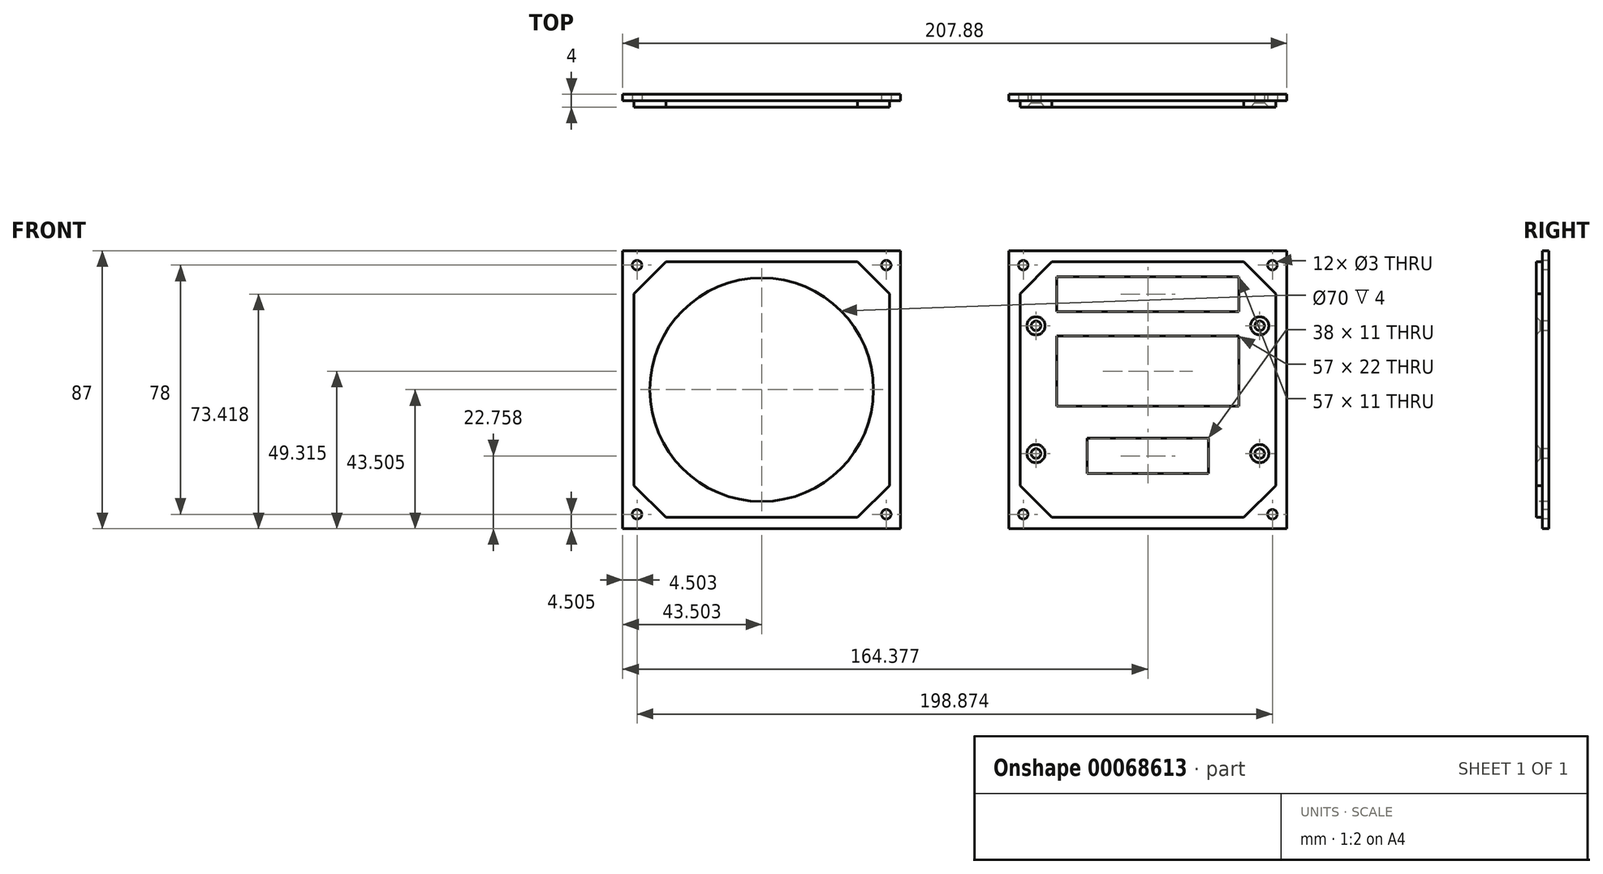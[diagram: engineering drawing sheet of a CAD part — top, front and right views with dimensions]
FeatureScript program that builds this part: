
annotation { "Feature Type Name" : "Feature", "Feature Type Description" : "" }
export const myFeature = defineFeature(function(context is Context, id is Id, definition is map)
    precondition{}
    {
        {
            var Q0;
            Q0=qCreatedBy(makeId("Front.planeOp"),FACE);
            cPlane(context, id + "F0", {"entities" : qUnion([Q0]), "cplaneType" : CPlaneType.OFFSET, "offset" : 5 * mm, "width" : 150 * mm, "height" : 150 * mm});
        }
        {
            var Q0;
            Q0=qCreatedBy(id+"F0.planeOp",FACE);
            var sketch = newSketch(context, id + "F1", { "sketchPlane" : qUnion([Q0])});
            skLineSegment(sketch, "E0.0", {"start": v(-50.26, 263.3) * mm, "end": v(-50.26, 233.3) * mm});
            skLineSegment(sketch, "E0.1", {"start": v(-50.26, 203.3) * mm, "end": v(-60.26, 193.3) * mm});
            skLineSegment(sketch, "E0.2", {"start": v(-60.26, 193.3) * mm, "end": v(-90.26, 193.3) * mm});
            skLineSegment(sketch, "E0.3", {"start": v(-120.26, 193.3) * mm, "end": v(-130.26, 203.3) * mm});
            skLineSegment(sketch, "E0.4", {"start": v(-130.26, 203.3) * mm, "end": v(-130.26, 233.3) * mm});
            skLineSegment(sketch, "E0.5", {"start": v(-130.26, 263.3) * mm, "end": v(-120.26, 273.3) * mm});
            skLineSegment(sketch, "E0.6", {"start": v(-120.26, 273.3) * mm, "end": v(-90.26, 273.3) * mm});
            skLineSegment(sketch, "E0.7", {"start": v(-60.26, 273.3) * mm, "end": v(-50.26, 263.3) * mm});
            skPoint(sketch, "E1", {"position": v(-90.26, 233.3) * mm});
            skLineSegment(sketch, "E2", {"start": v(-90.26, 273.3) * mm, "end": v(-60.26, 273.3) * mm});
            skLineSegment(sketch, "E3", {"start": v(-130.26, 233.3) * mm, "end": v(-130.26, 263.3) * mm});
            skLineSegment(sketch, "E4", {"start": v(-50.26, 233.3) * mm, "end": v(-50.26, 203.3) * mm});
            skLineSegment(sketch, "E5", {"start": v(-90.26, 193.3) * mm, "end": v(-120.26, 193.3) * mm});
            skSolve(sketch);
        }
        {
            var Q0;
            Q0=qSketchRegion(id+"F1",true);
            extrude(context, id + "F2", {"entities" : qUnion([Q0]), "depth" : 2 * mm});
        }
        {
            var Q0;
            Q0=makeQuery(id+"F2.opExtrude","CAP_FACE",FACE,{"disambiguationData":[OSD([sQuery(id+"F1.wireOp",EDGE,"E0.0"),sQuery(id+"F1.wireOp",EDGE,"E0.1"),sQuery(id+"F1.wireOp",EDGE,"E0.2"),sQuery(id+"F1.wireOp",EDGE,"E0.3"),sQuery(id+"F1.wireOp",EDGE,"E0.4"),sQuery(id+"F1.wireOp",EDGE,"E0.5"),sQuery(id+"F1.wireOp",EDGE,"E0.6"),sQuery(id+"F1.wireOp",EDGE,"E0.7"),sQuery(id+"F1.wireOp",EDGE,"E2"),sQuery(id+"F1.wireOp",EDGE,"E3"),sQuery(id+"F1.wireOp",EDGE,"E4"),sQuery(id+"F1.wireOp",EDGE,"E5")])],"isStart":true});
            var sketch = newSketch(context, id + "F3", { "sketchPlane" : qUnion([Q0])});
            skLineSegment(sketch, "E6.bottom", {"start": v(133.76, 276.8) * mm, "end": v(46.76, 276.8) * mm});
            skLineSegment(sketch, "E6.top", {"start": v(133.76, 189.8) * mm, "end": v(46.76, 189.8) * mm});
            skLineSegment(sketch, "E6.left", {"start": v(133.76, 276.8) * mm, "end": v(133.76, 189.8) * mm});
            skLineSegment(sketch, "E6.right", {"start": v(46.76, 276.8) * mm, "end": v(46.76, 189.8) * mm});
            skSolve(sketch);
        }
        {
            var Q0;
            Q0=qSketchRegion(id+"F3",true);
            extrude(context, id + "F4", {"entities" : qUnion([Q0]), "operationType" : NewBodyOperationType.ADD, "depth" : 2 * mm});
        }
        {
            var Q0;
            Q0=makeQuery(id+"F2.opExtrude","CAP_FACE",FACE,{"disambiguationData":[OSD([sQuery(id+"F1.wireOp",EDGE,"E0.0"),sQuery(id+"F1.wireOp",EDGE,"E0.1"),sQuery(id+"F1.wireOp",EDGE,"E0.2"),sQuery(id+"F1.wireOp",EDGE,"E0.3"),sQuery(id+"F1.wireOp",EDGE,"E0.4"),sQuery(id+"F1.wireOp",EDGE,"E0.5"),sQuery(id+"F1.wireOp",EDGE,"E0.6"),sQuery(id+"F1.wireOp",EDGE,"E0.7"),sQuery(id+"F1.wireOp",EDGE,"E2"),sQuery(id+"F1.wireOp",EDGE,"E3"),sQuery(id+"F1.wireOp",EDGE,"E4"),sQuery(id+"F1.wireOp",EDGE,"E5")])],"isStart":false});
            var sketch = newSketch(context, id + "F5", { "sketchPlane" : qUnion([Q0])});
            skCircle(sketch, "E7", {"center": v(-90.26, 233.3) * mm, "radius": 35 * mm});
            skCircle(sketch, "E8", {"center": v(-129.26, 272.3) * mm, "radius": 1.5 * mm});
            skCircle(sketch, "E9", {"center": v(-51.26, 272.3) * mm, "radius": 1.5 * mm});
            skCircle(sketch, "E10", {"center": v(-129.26, 194.3) * mm, "radius": 1.5 * mm});
            skCircle(sketch, "E11", {"center": v(-51.26, 194.3) * mm, "radius": 1.5 * mm});
            skSolve(sketch);
        }
        {
            var Q0;
            Q0=sQuery(id+"F5.wireOp",VERTEX,"E8.center");
            var Q1;
            Q1=sQuery(id+"F5.wireOp",VERTEX,"E9.center");
            var Q2;
            Q2=sQuery(id+"F5.wireOp",VERTEX,"E11.center");
            var Q3;
            Q3=sQuery(id+"F5.wireOp",VERTEX,"E10.center");
            var Q4;
            Q4=makeQuery(id+"F2.opExtrude","SWEPT_BODY",BODY,{"disambiguationData":[OSD([sQuery(id+"F1.wireOp",EDGE,"E0.0"),sQuery(id+"F1.wireOp",EDGE,"E0.1"),sQuery(id+"F1.wireOp",EDGE,"E0.2"),sQuery(id+"F1.wireOp",EDGE,"E0.3"),sQuery(id+"F1.wireOp",EDGE,"E0.4"),sQuery(id+"F1.wireOp",EDGE,"E0.5"),sQuery(id+"F1.wireOp",EDGE,"E0.6"),sQuery(id+"F1.wireOp",EDGE,"E0.7"),sQuery(id+"F1.wireOp",EDGE,"E2"),sQuery(id+"F1.wireOp",EDGE,"E3"),sQuery(id+"F1.wireOp",EDGE,"E4"),sQuery(id+"F1.wireOp",EDGE,"E5")])]});
            hole(context, id + "F6", {"style" : HoleStyle.SIMPLE, "endStyle" : HoleEndStyle.THROUGH, "holeDiameter" : 3 * mm, "locations" : qUnion([Q0, Q1, Q2, Q3]), "scope" : qUnion([Q4]), "isTappedThrough" : true});
        }
        {
            var Q0;
            Q0=sQuery(id+"F5.wireOp",VERTEX,"E7.center");
            var Q1;
            Q1=makeQuery(id+"F2.opExtrude","SWEPT_BODY",BODY,{"disambiguationData":[OSD([sQuery(id+"F1.wireOp",EDGE,"E0.0"),sQuery(id+"F1.wireOp",EDGE,"E0.1"),sQuery(id+"F1.wireOp",EDGE,"E0.2"),sQuery(id+"F1.wireOp",EDGE,"E0.3"),sQuery(id+"F1.wireOp",EDGE,"E0.4"),sQuery(id+"F1.wireOp",EDGE,"E0.5"),sQuery(id+"F1.wireOp",EDGE,"E0.6"),sQuery(id+"F1.wireOp",EDGE,"E0.7"),sQuery(id+"F1.wireOp",EDGE,"E2"),sQuery(id+"F1.wireOp",EDGE,"E3"),sQuery(id+"F1.wireOp",EDGE,"E4"),sQuery(id+"F1.wireOp",EDGE,"E5")])]});
            hole(context, id + "F7", {"style" : HoleStyle.SIMPLE, "endStyle" : HoleEndStyle.THROUGH, "holeDiameter" : 70 * mm, "locations" : qUnion([Q0]), "scope" : qUnion([Q1]), "isTappedThrough" : true});
        }
        {
            var Q0;
            Q0=qCreatedBy(id+"F0.planeOp",FACE);
            var sketch = newSketch(context, id + "F8", { "sketchPlane" : qUnion([Q0])});
            skLineSegment(sketch, "E12.0", {"start": v(70.62, 263.3) * mm, "end": v(70.62, 233.3) * mm});
            skLineSegment(sketch, "E12.1", {"start": v(70.62, 203.3) * mm, "end": v(60.62, 193.3) * mm});
            skLineSegment(sketch, "E12.2", {"start": v(60.62, 193.3) * mm, "end": v(30.62, 193.3) * mm});
            skLineSegment(sketch, "E12.3", {"start": v(0.62, 193.3) * mm, "end": v(-9.38, 203.3) * mm});
            skLineSegment(sketch, "E12.4", {"start": v(-9.38, 203.3) * mm, "end": v(-9.38, 233.3) * mm});
            skLineSegment(sketch, "E12.5", {"start": v(-9.38, 263.3) * mm, "end": v(0.62, 273.3) * mm});
            skLineSegment(sketch, "E12.6", {"start": v(0.62, 273.3) * mm, "end": v(30.62, 273.3) * mm});
            skLineSegment(sketch, "E12.7", {"start": v(60.62, 273.3) * mm, "end": v(70.62, 263.3) * mm});
            skPoint(sketch, "E13", {"position": v(30.62, 233.3) * mm});
            skLineSegment(sketch, "E14", {"start": v(30.62, 273.3) * mm, "end": v(60.62, 273.3) * mm});
            skLineSegment(sketch, "E15", {"start": v(-9.38, 233.3) * mm, "end": v(-9.38, 263.3) * mm});
            skLineSegment(sketch, "E16", {"start": v(70.62, 233.3) * mm, "end": v(70.62, 203.3) * mm});
            skLineSegment(sketch, "E17", {"start": v(30.62, 193.3) * mm, "end": v(0.62, 193.3) * mm});
            skSolve(sketch);
        }
        {
            var Q0;
            Q0 = qSketchRegion(id + "F8", true);
            extrude(context, id + "F9", {"entities" : qUnion([Q0]), "depth" : 2 * mm});
        }
        {
            var Q0;
            Q0=makeQuery(id+"F9.opExtrude","CAP_FACE",FACE,{"disambiguationData":[OSD([sQuery(id+"F8.wireOp",EDGE,"E12.0"),sQuery(id+"F8.wireOp",EDGE,"E12.1"),sQuery(id+"F8.wireOp",EDGE,"E12.2"),sQuery(id+"F8.wireOp",EDGE,"E12.3"),sQuery(id+"F8.wireOp",EDGE,"E12.4"),sQuery(id+"F8.wireOp",EDGE,"E12.5"),sQuery(id+"F8.wireOp",EDGE,"E12.6"),sQuery(id+"F8.wireOp",EDGE,"E12.7"),sQuery(id+"F8.wireOp",EDGE,"E14"),sQuery(id+"F8.wireOp",EDGE,"E15"),sQuery(id+"F8.wireOp",EDGE,"E16"),sQuery(id+"F8.wireOp",EDGE,"E17")])],"isStart":true});
            var sketch = newSketch(context, id + "F10", { "sketchPlane" : qUnion([Q0])});
            skLineSegment(sketch, "E18.bottom", {"start": v(-74.12, 189.8) * mm, "end": v(12.88, 189.8) * mm});
            skLineSegment(sketch, "E18.top", {"start": v(-74.12, 276.8) * mm, "end": v(12.88, 276.8) * mm});
            skLineSegment(sketch, "E18.left", {"start": v(-74.12, 189.8) * mm, "end": v(-74.12, 276.8) * mm});
            skLineSegment(sketch, "E18.right", {"start": v(12.88, 189.8) * mm, "end": v(12.88, 276.8) * mm});
            skPoint(sketch, "E18.middle", {"position": v(-30.62, 233.3) * mm});
            skSolve(sketch);
        }
        {
            var Q0;
            Q0 = qSketchRegion(id + "F10", true);
            extrude(context, id + "F11", {"entities" : qUnion([Q0]), "operationType" : NewBodyOperationType.ADD, "depth" : 2 * mm});
        }
        {
            var Q0;
            Q0=makeQuery(id+"F9.opExtrude","CAP_FACE",FACE,{"disambiguationData":[OSD([sQuery(id+"F8.wireOp",EDGE,"E12.0"),sQuery(id+"F8.wireOp",EDGE,"E12.1"),sQuery(id+"F8.wireOp",EDGE,"E12.2"),sQuery(id+"F8.wireOp",EDGE,"E12.3"),sQuery(id+"F8.wireOp",EDGE,"E12.4"),sQuery(id+"F8.wireOp",EDGE,"E12.5"),sQuery(id+"F8.wireOp",EDGE,"E12.6"),sQuery(id+"F8.wireOp",EDGE,"E12.7"),sQuery(id+"F8.wireOp",EDGE,"E14"),sQuery(id+"F8.wireOp",EDGE,"E15"),sQuery(id+"F8.wireOp",EDGE,"E16"),sQuery(id+"F8.wireOp",EDGE,"E17")])],"isStart":false});
            var sketch = newSketch(context, id + "F12", { "sketchPlane" : qUnion([Q0])});
            skCircle(sketch, "E19", {"center": v(30.62, 233.3) * mm, "radius": 30 * mm, "construction": true});
            skCircle(sketch, "E20", {"center": v(-8.38, 272.3) * mm, "radius": 1.5 * mm});
            skCircle(sketch, "E21", {"center": v(69.62, 272.3) * mm, "radius": 1.5 * mm});
            skCircle(sketch, "E22", {"center": v(-8.38, 194.3) * mm, "radius": 1.5 * mm});
            skCircle(sketch, "E23", {"center": v(69.62, 194.3) * mm, "radius": 1.5 * mm});
            skCircle(sketch, "E24", {"center": v(-4.38, 253.3) * mm, "radius": 1.5 * mm});
            skCircle(sketch, "E25", {"center": v(65.62, 253.3) * mm, "radius": 1.5 * mm});
            skCircle(sketch, "E26", {"center": v(-4.38, 213.3) * mm, "radius": 1.5 * mm});
            skCircle(sketch, "E27", {"center": v(65.62, 213.3) * mm, "radius": 1.5 * mm});
            skSolve(sketch);
        }
        {
            var Q0;
            Q0=sQuery(id+"F12.wireOp",VERTEX,"E20.center");
            var Q1;
            Q1=sQuery(id+"F12.wireOp",VERTEX,"E22.center");
            var Q2;
            Q2=sQuery(id+"F12.wireOp",VERTEX,"E23.center");
            var Q3;
            Q3=sQuery(id+"F12.wireOp",VERTEX,"E21.center");
            var Q4;
            Q4=makeQuery(id+"F9.opExtrude","SWEPT_BODY",BODY,{"disambiguationData":[OSD([sQuery(id+"F8.wireOp",EDGE,"E12.0"),sQuery(id+"F8.wireOp",EDGE,"E12.1"),sQuery(id+"F8.wireOp",EDGE,"E12.2"),sQuery(id+"F8.wireOp",EDGE,"E12.3"),sQuery(id+"F8.wireOp",EDGE,"E12.4"),sQuery(id+"F8.wireOp",EDGE,"E12.5"),sQuery(id+"F8.wireOp",EDGE,"E12.6"),sQuery(id+"F8.wireOp",EDGE,"E12.7"),sQuery(id+"F8.wireOp",EDGE,"E14"),sQuery(id+"F8.wireOp",EDGE,"E15"),sQuery(id+"F8.wireOp",EDGE,"E16"),sQuery(id+"F8.wireOp",EDGE,"E17")])]});
            hole(context, id + "F13", {"style" : HoleStyle.SIMPLE, "endStyle" : HoleEndStyle.THROUGH, "holeDiameter" : 3 * mm, "locations" : qUnion([Q0, Q1, Q2, Q3]), "scope" : qUnion([Q4]), "isTappedThrough" : true});
        }
        {
            var Q0;
            Q0=sQuery(id+"F12.wireOp",VERTEX,"E24.center");
            var Q1;
            Q1=sQuery(id+"F12.wireOp",VERTEX,"E26.center");
            var Q2;
            Q2=sQuery(id+"F12.wireOp",VERTEX,"E27.center");
            var Q3;
            Q3=sQuery(id+"F12.wireOp",VERTEX,"E25.center");
            var Q4;
            Q4=makeQuery(id+"F9.opExtrude","SWEPT_BODY",BODY,{"disambiguationData":[OSD([sQuery(id+"F8.wireOp",EDGE,"E12.0"),sQuery(id+"F8.wireOp",EDGE,"E12.1"),sQuery(id+"F8.wireOp",EDGE,"E12.2"),sQuery(id+"F8.wireOp",EDGE,"E12.3"),sQuery(id+"F8.wireOp",EDGE,"E12.4"),sQuery(id+"F8.wireOp",EDGE,"E12.5"),sQuery(id+"F8.wireOp",EDGE,"E12.6"),sQuery(id+"F8.wireOp",EDGE,"E12.7"),sQuery(id+"F8.wireOp",EDGE,"E14"),sQuery(id+"F8.wireOp",EDGE,"E15"),sQuery(id+"F8.wireOp",EDGE,"E16"),sQuery(id+"F8.wireOp",EDGE,"E17")])]});
            hole(context, id + "F14", {"style" : HoleStyle.C_SINK, "endStyle" : HoleEndStyle.THROUGH, "holeDiameter" : 3 * mm, "cSinkDiameter" : 5.7 * mm, "cSinkAngle" : 90 * degree, "locations" : qUnion([Q0, Q1, Q2, Q3]), "scope" : qUnion([Q4]), "isTappedThrough" : true});
        }
        {
            var Q0;
            Q0=makeQuery(id+"F12.imprint","IMPRINT",FACE,{"disambiguationData":[TD([[makeQuery(id+"F12.imprint","IMPRINT",EDGE,{"derivedFrom":sQuery(id+"F12.wireOp",EDGE,"E24")}),-1.0]])]});
            var sketch = newSketch(context, id + "F15", { "sketchPlane" : qUnion([Q0])});
            skLineSegment(sketch, "E28.bottom", {"start": v(20.12, 258.72) * mm, "end": v(3.12, 258.72) * mm, "construction": true});
            skLineSegment(sketch, "E28.top", {"start": v(20.12, 267.72) * mm, "end": v(3.12, 267.72) * mm, "construction": true});
            skLineSegment(sketch, "E28.left", {"start": v(20.12, 258.72) * mm, "end": v(20.12, 267.72) * mm, "construction": true});
            skLineSegment(sketch, "E28.right", {"start": v(3.12, 258.72) * mm, "end": v(3.12, 267.72) * mm, "construction": true});
            skPoint(sketch, "E28.middle", {"position": v(11.62, 263.22) * mm});
            skLineSegment(sketch, "E29.bottom", {"start": v(39.12, 258.72) * mm, "end": v(22.12, 258.72) * mm, "construction": true});
            skLineSegment(sketch, "E29.top", {"start": v(39.12, 267.72) * mm, "end": v(22.12, 267.72) * mm, "construction": true});
            skLineSegment(sketch, "E29.left", {"start": v(39.12, 258.72) * mm, "end": v(39.12, 267.72) * mm, "construction": true});
            skLineSegment(sketch, "E29.right", {"start": v(22.12, 258.72) * mm, "end": v(22.12, 267.72) * mm, "construction": true});
            skPoint(sketch, "E29.middle", {"position": v(30.62, 263.22) * mm});
            skLineSegment(sketch, "E30.bottom", {"start": v(58.12, 258.72) * mm, "end": v(41.12, 258.72) * mm, "construction": true});
            skLineSegment(sketch, "E30.top", {"start": v(58.12, 267.72) * mm, "end": v(41.12, 267.72) * mm, "construction": true});
            skLineSegment(sketch, "E30.left", {"start": v(58.12, 258.72) * mm, "end": v(58.12, 267.72) * mm, "construction": true});
            skLineSegment(sketch, "E30.right", {"start": v(41.12, 258.72) * mm, "end": v(41.12, 267.72) * mm, "construction": true});
            skPoint(sketch, "E30.middle", {"position": v(49.62, 263.22) * mm});
            skLineSegment(sketch, "E31.bottom", {"start": v(29.62, 208.06) * mm, "end": v(12.62, 208.06) * mm, "construction": true});
            skLineSegment(sketch, "E31.top", {"start": v(29.62, 217.06) * mm, "end": v(12.62, 217.06) * mm, "construction": true});
            skLineSegment(sketch, "E31.left", {"start": v(29.62, 208.06) * mm, "end": v(29.62, 217.06) * mm, "construction": true});
            skLineSegment(sketch, "E31.right", {"start": v(12.62, 208.06) * mm, "end": v(12.62, 217.06) * mm, "construction": true});
            skPoint(sketch, "E31.middle", {"position": v(21.12, 212.56) * mm});
            skLineSegment(sketch, "E32.bottom", {"start": v(48.62, 208.06) * mm, "end": v(31.62, 208.06) * mm, "construction": true});
            skLineSegment(sketch, "E32.top", {"start": v(48.62, 217.06) * mm, "end": v(31.62, 217.06) * mm, "construction": true});
            skLineSegment(sketch, "E32.left", {"start": v(48.62, 208.06) * mm, "end": v(48.62, 217.06) * mm, "construction": true});
            skLineSegment(sketch, "E32.right", {"start": v(31.62, 208.06) * mm, "end": v(31.62, 217.06) * mm, "construction": true});
            skPoint(sketch, "E32.middle", {"position": v(40.12, 212.56) * mm});
            skLineSegment(sketch, "E33.bottom", {"start": v(59.12, 257.72) * mm, "end": v(2.12, 257.72) * mm});
            skLineSegment(sketch, "E33.top", {"start": v(59.12, 268.72) * mm, "end": v(2.12, 268.72) * mm});
            skLineSegment(sketch, "E33.left", {"start": v(59.12, 257.72) * mm, "end": v(59.12, 268.72) * mm});
            skLineSegment(sketch, "E33.right", {"start": v(2.12, 257.72) * mm, "end": v(2.12, 268.72) * mm});
            skLineSegment(sketch, "E34.bottom", {"start": v(20.12, 240.12) * mm, "end": v(3.12, 240.12) * mm, "construction": true});
            skLineSegment(sketch, "E34.top", {"start": v(20.12, 249.12) * mm, "end": v(3.12, 249.12) * mm, "construction": true});
            skLineSegment(sketch, "E34.left", {"start": v(20.12, 240.12) * mm, "end": v(20.12, 249.12) * mm, "construction": true});
            skLineSegment(sketch, "E34.right", {"start": v(3.12, 240.12) * mm, "end": v(3.12, 249.12) * mm, "construction": true});
            skPoint(sketch, "E34.middle", {"position": v(11.62, 244.62) * mm});
            skLineSegment(sketch, "E35.bottom", {"start": v(39.12, 240.12) * mm, "end": v(22.12, 240.12) * mm, "construction": true});
            skLineSegment(sketch, "E35.top", {"start": v(39.12, 249.12) * mm, "end": v(22.12, 249.12) * mm, "construction": true});
            skLineSegment(sketch, "E35.left", {"start": v(39.12, 240.12) * mm, "end": v(39.12, 249.12) * mm, "construction": true});
            skLineSegment(sketch, "E35.right", {"start": v(22.12, 240.12) * mm, "end": v(22.12, 249.12) * mm, "construction": true});
            skPoint(sketch, "E35.middle", {"position": v(30.62, 244.62) * mm});
            skLineSegment(sketch, "E36.bottom", {"start": v(58.12, 240.12) * mm, "end": v(41.12, 240.12) * mm, "construction": true});
            skLineSegment(sketch, "E36.top", {"start": v(58.12, 249.12) * mm, "end": v(41.12, 249.12) * mm, "construction": true});
            skLineSegment(sketch, "E36.left", {"start": v(58.12, 240.12) * mm, "end": v(58.12, 249.12) * mm, "construction": true});
            skLineSegment(sketch, "E36.right", {"start": v(41.12, 240.12) * mm, "end": v(41.12, 249.12) * mm, "construction": true});
            skPoint(sketch, "E36.middle", {"position": v(49.62, 244.62) * mm});
            skLineSegment(sketch, "E37.top", {"start": v(20.12, 238.12) * mm, "end": v(3.12, 238.12) * mm, "construction": true});
            skLineSegment(sketch, "E37.left", {"start": v(20.12, 229.12) * mm, "end": v(20.12, 238.12) * mm, "construction": true});
            skLineSegment(sketch, "E37.right", {"start": v(3.12, 229.12) * mm, "end": v(3.12, 238.12) * mm, "construction": true});
            skPoint(sketch, "E37.middle", {"position": v(11.62, 233.62) * mm});
            skLineSegment(sketch, "E38.bottom", {"start": v(39.12, 229.12) * mm, "end": v(22.12, 229.12) * mm, "construction": true});
            skLineSegment(sketch, "E38.top", {"start": v(39.12, 238.12) * mm, "end": v(22.12, 238.12) * mm, "construction": true});
            skLineSegment(sketch, "E38.left", {"start": v(39.12, 229.12) * mm, "end": v(39.12, 238.12) * mm, "construction": true});
            skLineSegment(sketch, "E38.right", {"start": v(22.12, 229.12) * mm, "end": v(22.12, 238.12) * mm, "construction": true});
            skPoint(sketch, "E38.middle", {"position": v(30.62, 233.62) * mm});
            skLineSegment(sketch, "E39.bottom", {"start": v(58.12, 229.12) * mm, "end": v(41.12, 229.12) * mm, "construction": true});
            skLineSegment(sketch, "E39.top", {"start": v(58.12, 238.12) * mm, "end": v(41.12, 238.12) * mm, "construction": true});
            skLineSegment(sketch, "E39.left", {"start": v(58.12, 229.12) * mm, "end": v(58.12, 238.12) * mm, "construction": true});
            skLineSegment(sketch, "E39.right", {"start": v(41.12, 229.12) * mm, "end": v(41.12, 238.12) * mm, "construction": true});
            skPoint(sketch, "E39.middle", {"position": v(49.62, 233.62) * mm});
            skLineSegment(sketch, "E40", {"start": v(3.12, 229.12) * mm, "end": v(20.12, 229.12) * mm, "construction": true});
            skLineSegment(sketch, "E41.bottom", {"start": v(2.12, 250.12) * mm, "end": v(59.12, 250.12) * mm});
            skLineSegment(sketch, "E41.top", {"start": v(2.12, 228.12) * mm, "end": v(59.12, 228.12) * mm});
            skLineSegment(sketch, "E41.left", {"start": v(2.12, 250.12) * mm, "end": v(2.12, 228.12) * mm});
            skLineSegment(sketch, "E41.right", {"start": v(59.12, 250.12) * mm, "end": v(59.12, 228.12) * mm});
            skLineSegment(sketch, "E42.bottom", {"start": v(11.62, 218.06) * mm, "end": v(49.62, 218.06) * mm});
            skLineSegment(sketch, "E42.top", {"start": v(11.62, 207.06) * mm, "end": v(49.62, 207.06) * mm});
            skLineSegment(sketch, "E42.left", {"start": v(11.62, 218.06) * mm, "end": v(11.62, 207.06) * mm});
            skLineSegment(sketch, "E42.right", {"start": v(49.62, 218.06) * mm, "end": v(49.62, 207.06) * mm});
            skSolve(sketch);
        }
        {
            var Q0;
            Q0 = qSketchRegion(id + "F15", true);
            extrude(context, id + "F16", {"entities" : qUnion([Q0]), "operationType" : NewBodyOperationType.REMOVE, "oppositeDirection" : true, "depth" : 5 * mm});
        }
    });
